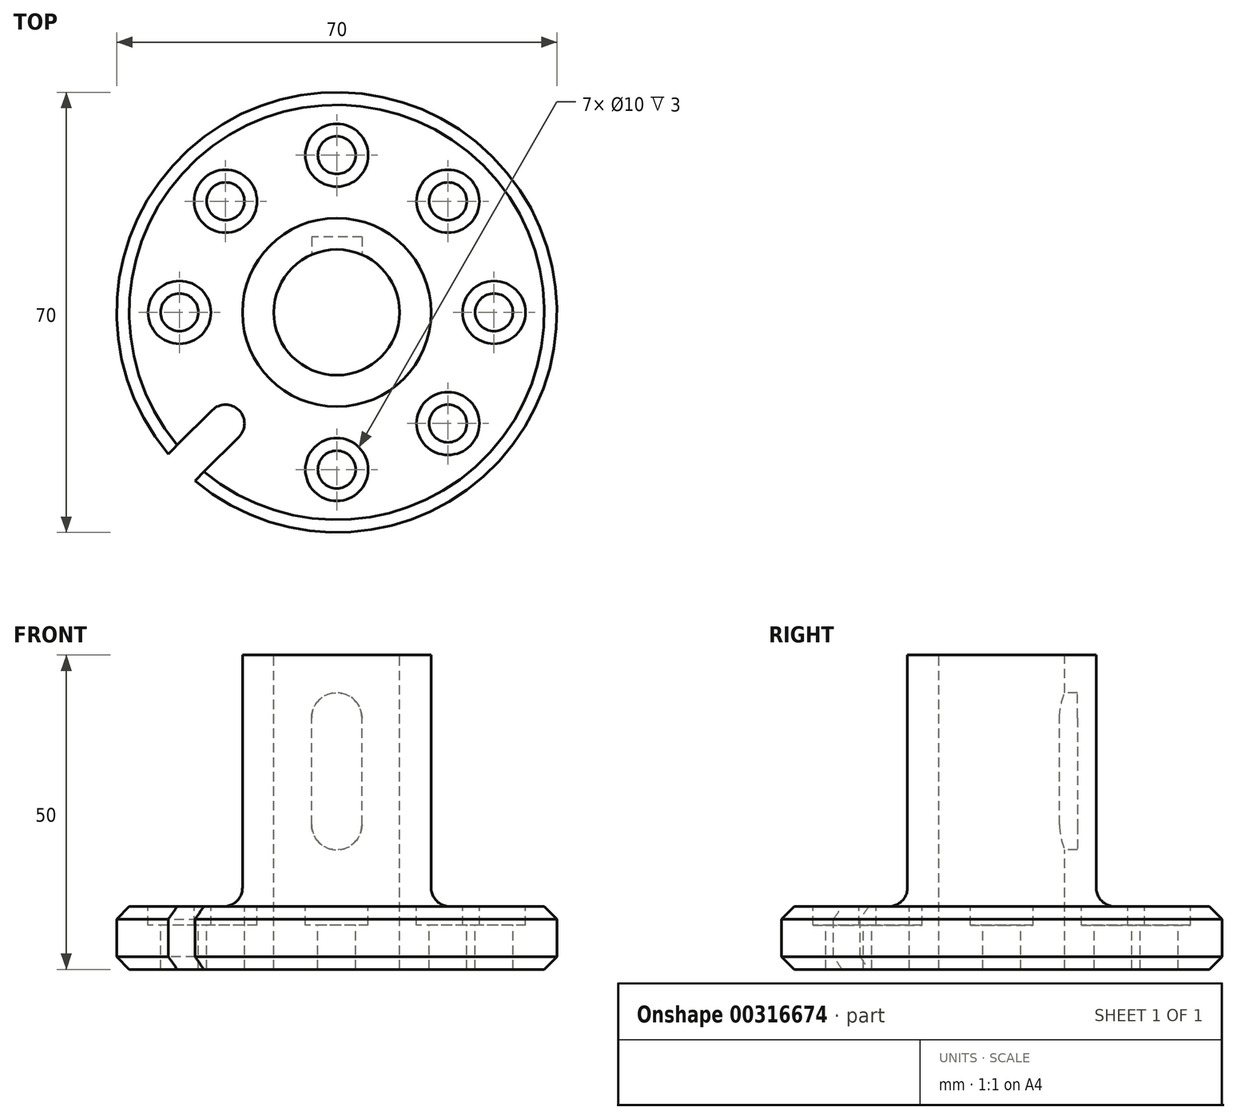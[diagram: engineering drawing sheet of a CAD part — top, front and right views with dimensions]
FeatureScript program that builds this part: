
annotation { "Feature Type Name" : "Feature", "Feature Type Description" : "" }
export const myFeature = defineFeature(function(context is Context, id is Id, definition is map)
    precondition{}
    {
        {
            var Q0;
            Q0=qCreatedBy(makeId("Front.planeOp"),FACE);
            var sketch = newSketch(context, id + "F0", { "sketchPlane" : qUnion([Q0])});
            skLineSegment(sketch, "E0", {"start": v(-10, 0) * mm, "end": v(-35, 0) * mm});
            skLineSegment(sketch, "E1", {"start": v(-35, 0) * mm, "end": v(-35, 10) * mm});
            skLineSegment(sketch, "E2", {"start": v(-35, 10) * mm, "end": v(-15, 10) * mm});
            skLineSegment(sketch, "E3", {"start": v(-15, 10) * mm, "end": v(-15, 50) * mm});
            skLineSegment(sketch, "E4", {"start": v(-15, 50) * mm, "end": v(-10, 50) * mm});
            skLineSegment(sketch, "E5", {"start": v(-10, 50) * mm, "end": v(-10, 0) * mm});
            skLineSegment(sketch, "E6", {"start": v(0, 50) * mm, "end": v(0, 0) * mm, "construction": true});
            skSolve(sketch);
        }
        {
            var Q0;
            Q0=makeQuery(id+"F0.imprint","IMPRINT",FACE,{"disambiguationData":[TD([[makeQuery(id+"F0.imprint","IMPRINT",EDGE,{"derivedFrom":sQuery(id+"F0.wireOp",EDGE,"E0")}),-1.0]])]});
            var Q1;
            Q1=sQuery(id+"F0.wireOp",EDGE,"E2");
            var Q2;
            Q2=sQuery(id+"F0.wireOp",EDGE,"E0");
            var Q3;
            Q3=sQuery(id+"F0.wireOp",EDGE,"E5");
            var Q4;
            Q4=sQuery(id+"F0.wireOp",EDGE,"E4");
            var Q5;
            Q5=sQuery(id+"F0.wireOp",EDGE,"E1");
            var Q6;
            Q6=sQuery(id+"F0.wireOp",EDGE,"E3");
            var Q7;
            Q7=sQuery(id+"F0.wireOp",EDGE,"E6");
            revolve(context, id + "F1", {"entities" : qUnion([Q0]), "surfaceEntities" : qUnion([Q1, Q2, Q3, Q4, Q5, Q6]), "axis" : qUnion([Q7]), "revolveType" : RevolveType.FULL});
        }
        {
            var Q0;
            Q0=makeQuery(id+"F1.opRevolve","SWEPT_FACE",FACE,{"disambiguationData":[OSD([sQuery(id+"F0.wireOp",EDGE,"E2")])]});
            var sketch = newSketch(context, id + "F2", { "sketchPlane" : qUnion([Q0])});
            skPoint(sketch, "E7", {"position": v(0, 25) * mm});
            skPoint(sketch, "E8.1.0", {"position": v(-17.68, 17.68) * mm});
            skPoint(sketch, "E8.2.0", {"position": v(-25, 0) * mm});
            skPoint(sketch, "E8.3.0", {"position": v(-17.68, -17.68) * mm});
            skPoint(sketch, "E8.4.0", {"position": v(0, -25) * mm});
            skPoint(sketch, "E8.5.0", {"position": v(17.68, -17.68) * mm});
            skPoint(sketch, "E8.6.0", {"position": v(25, 0) * mm});
            skPoint(sketch, "E8.7.0", {"position": v(17.68, 17.68) * mm});
            skPoint(sketch, "E8.center", {"position": v(0, 0) * mm});
            skCircle(sketch, "E9", {"center": v(-17.68, -17.68) * mm, "radius": 3 * mm});
            skLineSegment(sketch, "E10", {"start": v(-19.8, -15.56) * mm, "end": v(-26.78, -22.54) * mm});
            skLineSegment(sketch, "E11", {"start": v(-22.54, -26.78) * mm, "end": v(-15.56, -19.8) * mm});
            skSolve(sketch);
        }
        {
            var Q0;
            Q0=sQuery(id+"F2.wireOp",VERTEX,"E8.1.0");
            var Q1;
            Q1=sQuery(id+"F2.wireOp",VERTEX,"E7");
            var Q2;
            Q2=sQuery(id+"F2.wireOp",VERTEX,"E8.7.0");
            var Q3;
            Q3=sQuery(id+"F2.wireOp",VERTEX,"E8.6.0");
            var Q4;
            Q4=sQuery(id+"F2.wireOp",VERTEX,"E8.4.0");
            var Q5;
            Q5=sQuery(id+"F2.wireOp",VERTEX,"E8.2.0");
            var Q6;
            Q6=sQuery(id+"F2.wireOp",VERTEX,"E8.5.0");
            var Q7;
            Q7=makeQuery(id+"F1.opRevolve","SWEPT_BODY",BODY,{"disambiguationData":[OSD([sQuery(id+"F0.wireOp",EDGE,"E0"),sQuery(id+"F0.wireOp",EDGE,"E1"),sQuery(id+"F0.wireOp",EDGE,"E2"),sQuery(id+"F0.wireOp",EDGE,"E3"),sQuery(id+"F0.wireOp",EDGE,"E4"),sQuery(id+"F0.wireOp",EDGE,"E5")])]});
            hole(context, id + "F3", {"style" : HoleStyle.C_BORE, "endStyle" : HoleEndStyle.THROUGH, "holeDiameter" : 6 * mm, "cBoreDiameter" : 10 * mm, "cBoreDepth" : 3 * mm, "tappedDepth" : 12 * mm, "tapClearance" : 3, "startFromSketch" : true, "locations" : qUnion([Q0, Q1, Q2, Q3, Q4, Q5, Q6]), "scope" : qUnion([Q7])});
        }
        {
            var Q0;
            {var subQ0=sQuery(id+"F2.wireOp",EDGE,"E10");Q0=makeQuery(id+"F2.imprint","IMPRINT",FACE,{"disambiguationData":[TD([[makeQuery(id+"F2.imprint","IMPRINT",EDGE,{"derivedFrom":subQ0}),1.0]])]});}
            var Q1;
            {var subQ0=sQuery(id+"F2.wireOp",EDGE,"E9");var subQ1=makeQuery(id+"F2.imprint","INTERSECT",VERTEX,{"derivedFrom":[subQ0,sQuery(id+"F2.wireOp",EDGE,"E10")]});Q1=makeQuery(id+"F2.imprint","IMPRINT",FACE,{"disambiguationData":[TD([[makeQuery(id+"F2.imprint","IMPRINT",EDGE,{"disambiguationData":[TD([[subQ1,-1.0]])],"derivedFrom":subQ0}),1.0]])]});}
            extrude(context, id + "F4", {"entities" : qUnion([Q0, Q1]), "operationType" : NewBodyOperationType.REMOVE, "endBound" : BoundingType.THROUGH_ALL, "oppositeDirection" : true, "depth" : 25 * mm});
        }
        {
            var Q0;
            Q0=qCreatedBy(makeId("Front.planeOp"),FACE);
            var sketch = newSketch(context, id + "F5", { "sketchPlane" : qUnion([Q0])});
            skCircle(sketch, "E12", {"center": v(0, 40) * mm, "radius": 4 * mm});
            skCircle(sketch, "E13", {"center": v(0, 23) * mm, "radius": 4 * mm});
            skLineSegment(sketch, "E14", {"start": v(-4, 40) * mm, "end": v(-4, 23) * mm});
            skLineSegment(sketch, "E15", {"start": v(4, 40) * mm, "end": v(4, 23) * mm});
            skSolve(sketch);
        }
        {
            var Q0;
            Q0 = qSketchRegion(id + "F5", true);
            extrude(context, id + "F6", {"entities" : qUnion([Q0]), "operationType" : NewBodyOperationType.REMOVE, "oppositeDirection" : true, "depth" : 12 * mm});
        }
        {
            var Q0;
            Q0=makeQuery(id+"F1.opRevolve","SWEPT_EDGE",EDGE,{"disambiguationData":[OSD([sQuery(id+"F0.wireOp",EDGE,"E2"),sQuery(id+"F0.wireOp",EDGE,"E3")])]});
            fillet(context, id + "F7", {"entities" : qUnion([Q0]), "radius" : 3 * mm, "tangentPropagation" : true, "allowEdgeOverflow" : false});
        }
        {
            var Q0;
            Q0=makeQuery(id+"F1.opRevolve","SWEPT_EDGE",EDGE,{"disambiguationData":[OSD([sQuery(id+"F0.wireOp",EDGE,"E1"),sQuery(id+"F0.wireOp",EDGE,"E2")])]});
            var Q1;
            Q1=makeQuery(id+"F1.opRevolve","SWEPT_EDGE",EDGE,{"disambiguationData":[OSD([sQuery(id+"F0.wireOp",EDGE,"E0"),sQuery(id+"F0.wireOp",EDGE,"E1")])]});
            chamfer(context, id + "F8", {"entities" : qUnion([Q0, Q1]), "width" : 2 * mm, "tangentPropagation" : true});
        }
    });
